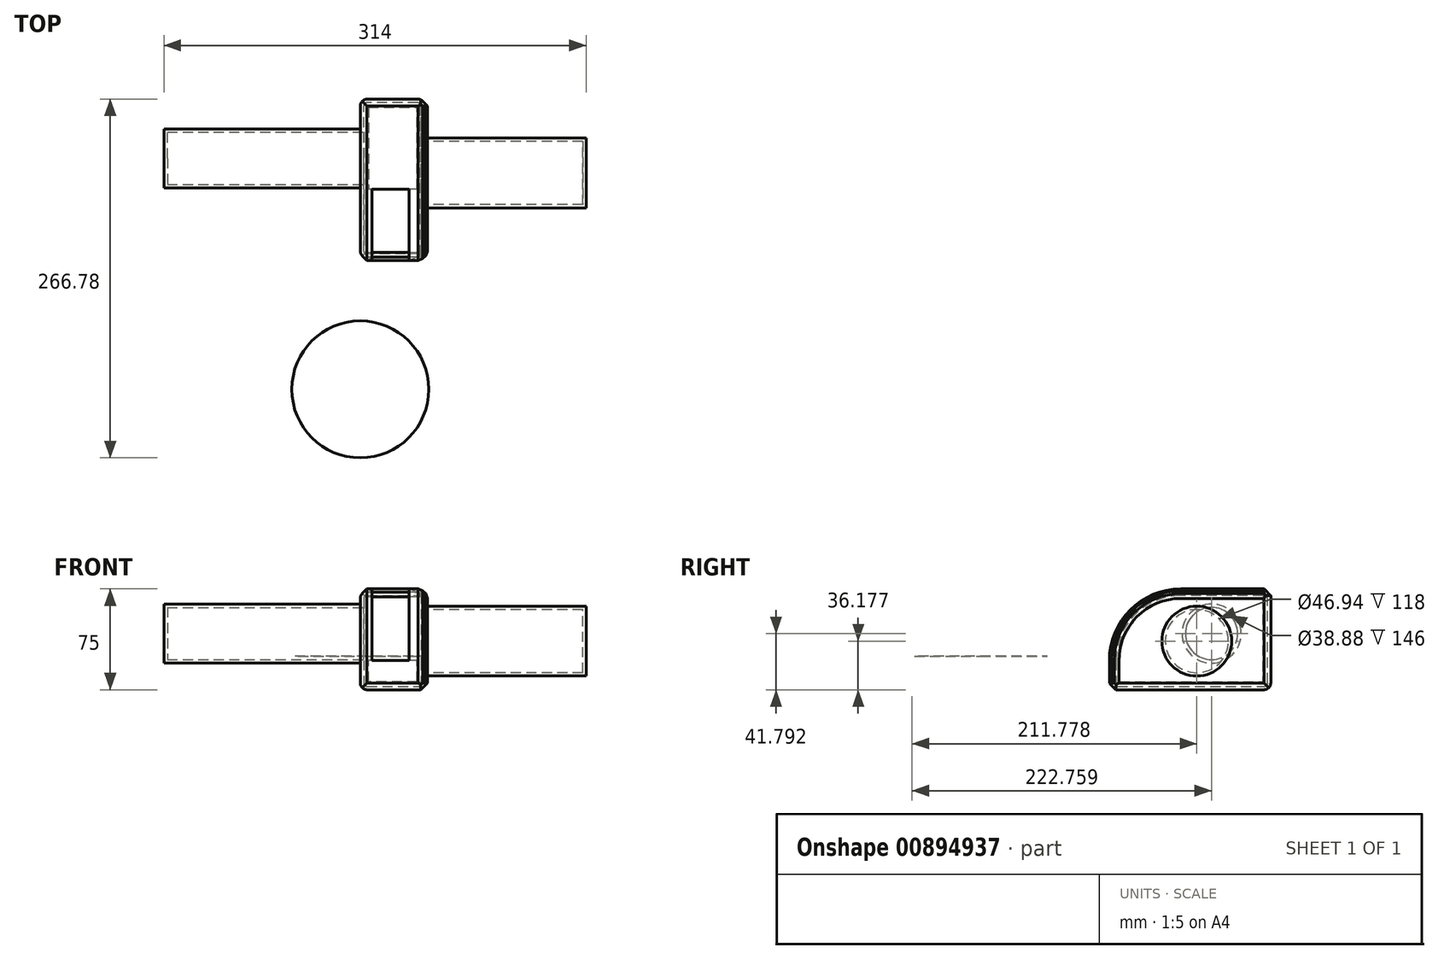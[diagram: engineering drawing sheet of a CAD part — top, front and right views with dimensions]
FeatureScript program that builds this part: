
annotation { "Feature Type Name" : "Feature", "Feature Type Description" : "" }
export const myFeature = defineFeature(function(context is Context, id is Id, definition is map)
    precondition{}
    {
        {
            var Q0;
            Q0=qCreatedBy(makeId("Top.planeOp"),FACE);
            var sketch = newSketch(context, id + "F0", { "sketchPlane" : qUnion([Q0])});
            skLineSegment(sketch, "E0.bottom", {"start": v(0, 164.93) * mm, "end": v(50, 164.93) * mm});
            skLineSegment(sketch, "E0.top", {"start": v(0, 44.93) * mm, "end": v(50, 44.93) * mm});
            skLineSegment(sketch, "E0.left", {"start": v(0, 164.93) * mm, "end": v(0, 44.93) * mm});
            skLineSegment(sketch, "E0.right", {"start": v(50, 164.93) * mm, "end": v(50, 44.93) * mm});
            skSolve(sketch);
        }
        {
            var Q0;
            Q0=makeQuery(id+"F0.imprint","IMPRINT",FACE,{"disambiguationData":[TD([[makeQuery(id+"F0.imprint","IMPRINT",EDGE,{"derivedFrom":sQuery(id+"F0.wireOp",EDGE,"E0.bottom")}),-1.0]])]});
            extrude(context, id + "F1", {"entities" : qUnion([Q0]), "depth" : 75 * mm, "offsetDistance" : 25 * mm});
        }
        {
            var Q0;
            Q0=makeQuery(id+"F1.opExtrude","CAP_EDGE",EDGE,{"disambiguationData":[OSD([sQuery(id+"F0.wireOp",EDGE,"E0.top")])],"isStart":false});
            fillet(context, id + "F2", {"entities" : qUnion([Q0]), "radius" : 53.1 * mm, "tangentPropagation" : true, "allowEdgeOverflow" : false});
        }
        {
            var Q0;
            Q0=makeQuery(id+"F2.opFillet","BLEND_EDGE",EDGE,{"blendedFrom":[makeQuery(id+"F1.opExtrude","CAP_EDGE",EDGE,{"disambiguationData":[OSD([sQuery(id+"F0.wireOp",EDGE,"E0.top")])],"isStart":false}),makeQuery(id+"F1.opExtrude","SWEPT_FACE",FACE,{"disambiguationData":[OSD([sQuery(id+"F0.wireOp",EDGE,"E0.right")])]})],"blendedInto":[makeQuery(id+"F1.opExtrude","SWEPT_FACE",FACE,{"disambiguationData":[OSD([sQuery(id+"F0.wireOp",EDGE,"E0.right")])]})]});
            var Q1;
            Q1=makeQuery(id+"F1.opExtrude","SWEPT_EDGE",EDGE,{"disambiguationData":[OSD([sQuery(id+"F0.wireOp",EDGE,"E0.bottom"),sQuery(id+"F0.wireOp",EDGE,"E0.right")])]});
            var Q2;
            Q2=makeQuery(id+"F1.opExtrude","CAP_EDGE",EDGE,{"disambiguationData":[OSD([sQuery(id+"F0.wireOp",EDGE,"E0.right")])],"isStart":true});
            var Q3;
            {var subQ0=sQuery(id+"F0.wireOp",EDGE,"E0.top");Q3=makeQuery(id+"F2.opFillet","BLEND_EDGE",EDGE,{"blendedFrom":[makeQuery(id+"F1.opExtrude","CAP_EDGE",EDGE,{"disambiguationData":[OSD([subQ0])],"isStart":false}),makeQuery(id+"F1.opExtrude","SWEPT_FACE",FACE,{"disambiguationData":[OSD([subQ0])]})],"blendedInto":[makeQuery(id+"F1.opExtrude","SWEPT_FACE",FACE,{"disambiguationData":[OSD([subQ0])]})]});}
            var Q4;
            Q4=makeQuery(id+"F1.opExtrude","CAP_EDGE",EDGE,{"disambiguationData":[OSD([sQuery(id+"F0.wireOp",EDGE,"E0.top")])],"isStart":true});
            var Q5;
            Q5=makeQuery(id+"F1.opExtrude","CAP_EDGE",EDGE,{"disambiguationData":[OSD([sQuery(id+"F0.wireOp",EDGE,"E0.bottom")])],"isStart":false});
            var Q6;
            {var subQ0=sQuery(id+"F0.wireOp",EDGE,"E0.top");Q6=makeQuery(id+"F2.opFillet","BLEND_EDGE",EDGE,{"blendedFrom":[makeQuery(id+"F1.opExtrude","CAP_EDGE",EDGE,{"disambiguationData":[OSD([subQ0])],"isStart":false}),makeQuery(id+"F1.opExtrude","CAP_FACE",FACE,{"disambiguationData":[OSD([sQuery(id+"F0.wireOp",EDGE,"E0.bottom"),subQ0,sQuery(id+"F0.wireOp",EDGE,"E0.left"),sQuery(id+"F0.wireOp",EDGE,"E0.right")])],"isStart":false})],"blendedInto":[makeQuery(id+"F1.opExtrude","CAP_FACE",FACE,{"disambiguationData":[OSD([sQuery(id+"F0.wireOp",EDGE,"E0.bottom"),subQ0,sQuery(id+"F0.wireOp",EDGE,"E0.left"),sQuery(id+"F0.wireOp",EDGE,"E0.right")])],"isStart":false})]});}
            var Q7;
            Q7=makeQuery(id+"F2.opFillet","BLEND_EDGE",EDGE,{"blendedFrom":[makeQuery(id+"F1.opExtrude","CAP_EDGE",EDGE,{"disambiguationData":[OSD([sQuery(id+"F0.wireOp",EDGE,"E0.top")])],"isStart":false}),makeQuery(id+"F1.opExtrude","SWEPT_FACE",FACE,{"disambiguationData":[OSD([sQuery(id+"F0.wireOp",EDGE,"E0.left")])]})],"blendedInto":[makeQuery(id+"F1.opExtrude","SWEPT_FACE",FACE,{"disambiguationData":[OSD([sQuery(id+"F0.wireOp",EDGE,"E0.left")])]})]});
            chamfer(context, id + "F3", {"entities" : qUnion([Q0, Q1, Q2, Q3, Q4, Q5, Q6, Q7]), "width" : 5 * mm, "tangentPropagation" : true});
        }
        {
            var Q0;
            Q0=makeQuery(id+"F1.opExtrude","SWEPT_EDGE",EDGE,{"disambiguationData":[OSD([sQuery(id+"F0.wireOp",EDGE,"E0.bottom"),sQuery(id+"F0.wireOp",EDGE,"E0.left")])]});
            var Q1;
            Q1=makeQuery(id+"F1.opExtrude","CAP_EDGE",EDGE,{"disambiguationData":[OSD([sQuery(id+"F0.wireOp",EDGE,"E0.left")])],"isStart":true});
            var Q2;
            {var subQ0=sQuery(id+"F0.wireOp",EDGE,"E0.left");Q2=makeQuery(id+"F3.opChamfer","BLEND_EDGE",EDGE,{"blendedFrom":[makeQuery(id+"F1.opExtrude","CAP_EDGE",EDGE,{"disambiguationData":[OSD([subQ0])],"isStart":false}),makeQuery(id+"F1.opExtrude","SWEPT_FACE",FACE,{"disambiguationData":[OSD([subQ0])]})],"blendedInto":[makeQuery(id+"F1.opExtrude","SWEPT_FACE",FACE,{"disambiguationData":[OSD([subQ0])]})]});}
            var Q3;
            Q3=makeQuery(id+"F1.opExtrude","SWEPT_FACE",FACE,{"disambiguationData":[OSD([sQuery(id+"F0.wireOp",EDGE,"E0.left")])]});
            var Q4;
            {var subQ0=sQuery(id+"F0.wireOp",EDGE,"E0.bottom");Q4=makeQuery(id+"F3.opChamfer","BLEND_EDGE",EDGE,{"blendedFrom":[makeQuery(id+"F1.opExtrude","SWEPT_EDGE",EDGE,{"disambiguationData":[OSD([subQ0,sQuery(id+"F0.wireOp",EDGE,"E0.right")])]}),makeQuery(id+"F1.opExtrude","SWEPT_FACE",FACE,{"disambiguationData":[OSD([subQ0])]})],"blendedInto":[makeQuery(id+"F1.opExtrude","SWEPT_FACE",FACE,{"disambiguationData":[OSD([subQ0])]})]});}
            var Q5;
            Q5=makeQuery(id+"F1.opExtrude","CAP_EDGE",EDGE,{"disambiguationData":[OSD([sQuery(id+"F0.wireOp",EDGE,"E0.bottom")])],"isStart":true});
            fillet(context, id + "F4", {"entities" : qUnion([Q0, Q1, Q2, Q3, Q4, Q5]), "radius" : 5 * mm, "tangentPropagation" : true, "allowEdgeOverflow" : false});
        }
        {
            var Q0;
            {var subQ0=sQuery(id+"F0.wireOp",EDGE,"E0.right");Q0=makeQuery(id+"F3.opChamfer","BLEND_EDGE",EDGE,{"blendedFrom":[makeQuery(id+"F1.opExtrude","CAP_EDGE",EDGE,{"disambiguationData":[OSD([subQ0])],"isStart":false}),makeQuery(id+"F1.opExtrude","SWEPT_FACE",FACE,{"disambiguationData":[OSD([subQ0])]})],"blendedInto":[makeQuery(id+"F1.opExtrude","SWEPT_FACE",FACE,{"disambiguationData":[OSD([subQ0])]})]});}
            var Q1;
            {var subQ0=sQuery(id+"F0.wireOp",EDGE,"E0.right");Q1=makeQuery(id+"F3.opChamfer","BLEND_EDGE",EDGE,{"blendedFrom":[makeQuery(id+"F1.opExtrude","CAP_EDGE",EDGE,{"disambiguationData":[OSD([subQ0])],"isStart":false}),makeQuery(id+"F1.opExtrude","CAP_FACE",FACE,{"disambiguationData":[OSD([sQuery(id+"F0.wireOp",EDGE,"E0.bottom"),sQuery(id+"F0.wireOp",EDGE,"E0.top"),sQuery(id+"F0.wireOp",EDGE,"E0.left"),subQ0])],"isStart":false})],"blendedInto":[makeQuery(id+"F1.opExtrude","CAP_FACE",FACE,{"disambiguationData":[OSD([sQuery(id+"F0.wireOp",EDGE,"E0.bottom"),sQuery(id+"F0.wireOp",EDGE,"E0.top"),sQuery(id+"F0.wireOp",EDGE,"E0.left"),subQ0])],"isStart":false})]});}
            chamfer(context, id + "F5", {"entities" : qUnion([Q0, Q1]), "width" : 5 * mm, "tangentPropagation" : true});
        }
        {
            var Q0;
            Q0=makeQuery(id+"F1.opExtrude","SWEPT_FACE",FACE,{"disambiguationData":[OSD([sQuery(id+"F0.wireOp",EDGE,"E0.right")])]});
            var sketch = newSketch(context, id + "F6", { "sketchPlane" : qUnion([Q0])});
            skCircle(sketch, "E1", {"center": v(109.93, 36.18) * mm, "radius": 25.97 * mm});
            skSolve(sketch);
        }
        {
            var Q0;
            Q0=makeQuery(id+"F6.imprint","IMPRINT",FACE,{"disambiguationData":[TD([[makeQuery(id+"F6.imprint","IMPRINT",EDGE,{"derivedFrom":sQuery(id+"F6.wireOp",EDGE,"E1")}),1.0]])]});
            extrude(context, id + "F7", {"entities" : qUnion([Q0]), "operationType" : NewBodyOperationType.ADD, "depth" : 118 * mm, "offsetDistance" : 25 * mm});
        }
        {
            var Q0;
            Q0=makeQuery(id+"F1.opExtrude","SWEPT_FACE",FACE,{"disambiguationData":[OSD([sQuery(id+"F0.wireOp",EDGE,"E0.left")])]});
            var sketch = newSketch(context, id + "F8", { "sketchPlane" : qUnion([Q0])});
            skCircle(sketch, "E2", {"center": v(-120.9, 41.8) * mm, "radius": 21.94 * mm});
            skSolve(sketch);
        }
        {
            var Q0;
            Q0=makeQuery(id+"F8.imprint","IMPRINT",FACE,{"disambiguationData":[TD([[makeQuery(id+"F8.imprint","IMPRINT",EDGE,{"derivedFrom":sQuery(id+"F8.wireOp",EDGE,"E2")}),1.0]])]});
            extrude(context, id + "F9", {"entities" : qUnion([Q0]), "operationType" : NewBodyOperationType.ADD, "depth" : 25 * mm, "offsetDistance" : 25 * mm});
        }
        {
            var Q0;
            Q0=makeQuery(id+"F9.opExtrude","CAP_FACE",FACE,{"disambiguationData":[OSD([sQuery(id+"F8.wireOp",EDGE,"E2")])],"isStart":false});
            var sketch = newSketch(context, id + "F10", { "sketchPlane" : qUnion([Q0])});
            skSolve(sketch);
        }
        {
            var Q0;
            Q0 = qSketchRegion(id + "F10", true);
            var Q1;
            Q1=makeQuery(id+"F10.imprint","IMPRINT",FACE,{"disambiguationData":[TD([[makeQuery(id+"F10.imprint","IMPRINT",EDGE,{"derivedFrom":makeQuery(id+"F9.opExtrude","CAP_EDGE",EDGE,{"disambiguationData":[OSD([sQuery(id+"F8.wireOp",EDGE,"E2")])],"isStart":false})}),1.0]])]});
            extrude(context, id + "F11", {"entities" : qUnion([Q0, Q1]), "operationType" : NewBodyOperationType.ADD, "depth" : 121 * mm, "offsetDistance" : 25 * mm});
        }
        {
            var Q0;
            Q0=makeQuery(id+"F2.opFillet","BLEND_FACE",FACE,{"disambiguationData":[OSD([sQuery(id+"F0.wireOp",EDGE,"E0.top")])]});
            shell(context, id + "F12", {"entities" : qUnion([Q0]), "thickness" : 2.5 * mm});
        }
        {
            var Q0;
            Q0=qCreatedBy(makeId("Right.planeOp"),FACE);
            var sketch = newSketch(context, id + "F13", { "sketchPlane" : qUnion([Q0])});
            skLineSegment(sketch, "E3", {"start": v(-50.92, 45.68) * mm, "end": v(-50.92, -6.78) * mm});
            skArc(sketch, "E4", {"start": v(0, 24.8) * mm, "mid": v(-9.9, 73.2) * mm, "end": v(-50.92, 45.68) * mm});
            skArc(sketch, "E5", {"start": v(-50.92, -6.78) * mm, "mid": v(2.9, -36.74) * mm, "end": v(0, 24.8) * mm});
            skSolve(sketch);
        }
        {
            var Q0;
            Q0=makeQuery(id+"F13.imprint","IMPRINT",FACE,{"disambiguationData":[TD([[makeQuery(id+"F13.imprint","IMPRINT",EDGE,{"derivedFrom":sQuery(id+"F13.wireOp",EDGE,"E3")}),1.0]])]});
            var Q1;
            Q1=sQuery(id+"F13.wireOp",EDGE,"E3");
            revolve(context, id + "F14", {"surfaceOperationType" : NewSurfaceOperationType.NEW, "entities" : qUnion([Q0]), "axis" : qUnion([Q1]), "revolveType" : RevolveType.FULL});
        }
    });
